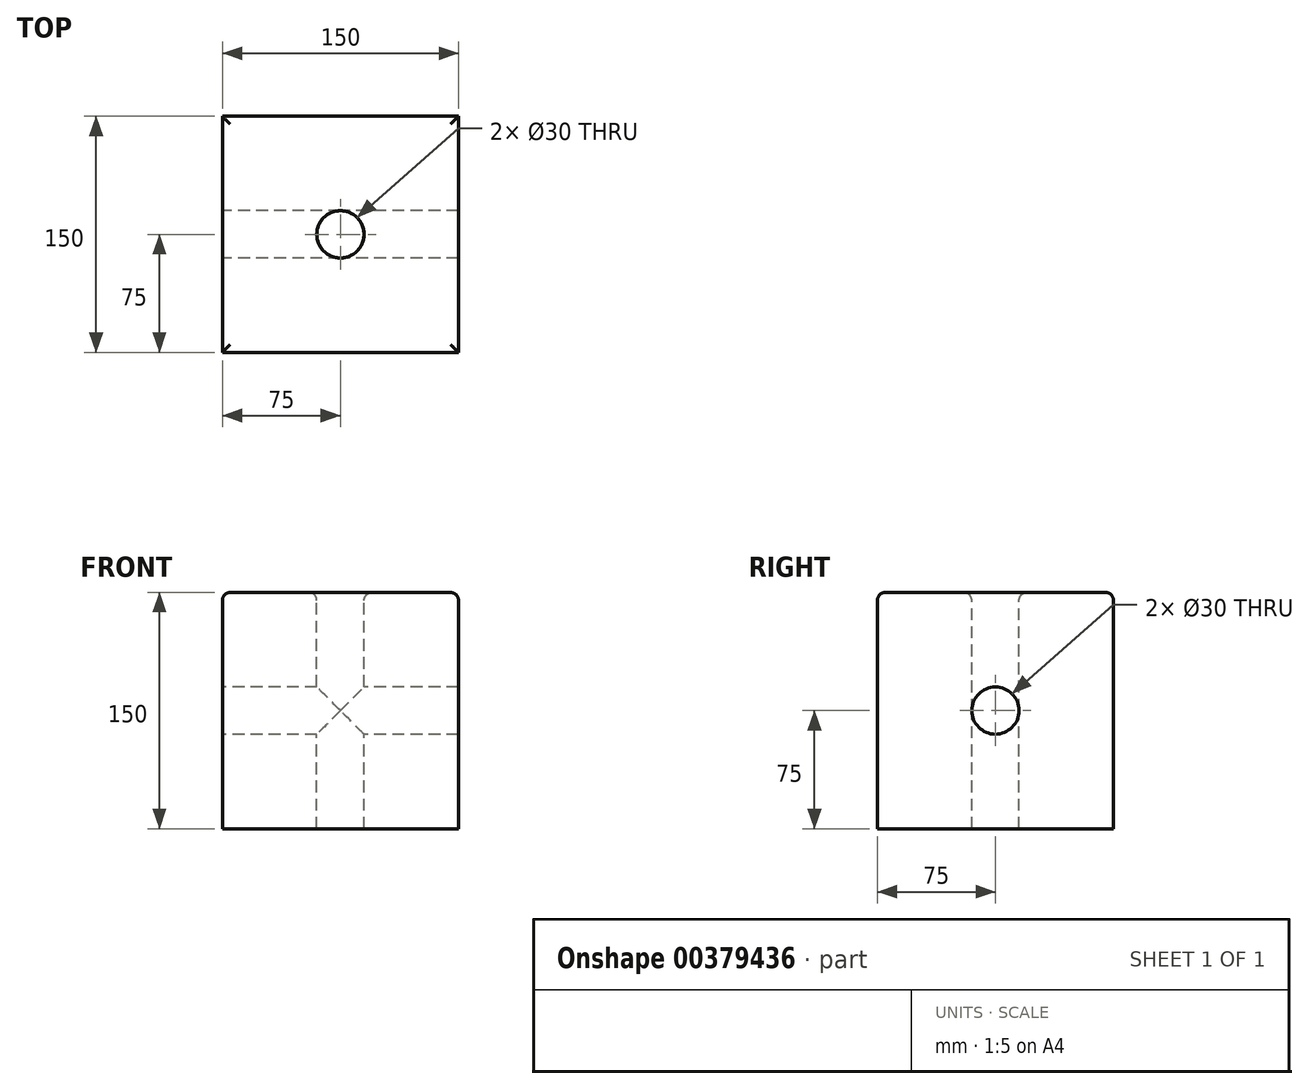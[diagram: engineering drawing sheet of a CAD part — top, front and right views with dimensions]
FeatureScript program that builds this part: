
annotation { "Feature Type Name" : "Feature", "Feature Type Description" : "" }
export const myFeature = defineFeature(function(context is Context, id is Id, definition is map)
    precondition{}
    {
        {
            var Q0;
            Q0=qCreatedBy(makeId("Front.planeOp"),FACE);
            var sketch = newSketch(context, id + "F0", { "sketchPlane" : qUnion([Q0])});
            skLineSegment(sketch, "E0.bottom", {"start": v(75, 75) * mm, "end": v(-75, 75) * mm});
            skLineSegment(sketch, "E0.top", {"start": v(75, -75) * mm, "end": v(-75, -75) * mm});
            skLineSegment(sketch, "E0.left", {"start": v(75, 75) * mm, "end": v(75, -75) * mm});
            skLineSegment(sketch, "E0.right", {"start": v(-75, 75) * mm, "end": v(-75, -75) * mm});
            skPoint(sketch, "E0.middle", {"position": v(0, 0) * mm});
            skSolve(sketch);
        }
        {
            var Q0;
            Q0 = qSketchRegion(id + "F0", true);
            extrude(context, id + "F1", {"entities" : qUnion([Q0]), "depth" : 150 * mm});
        }
        {
            var Q0;
            Q0=makeQuery(id+"F1.opExtrude","SWEPT_FACE",FACE,{"disambiguationData":[OSD([sQuery(id+"F0.wireOp",EDGE,"E0.bottom")])]});
            var sketch = newSketch(context, id + "F2", { "sketchPlane" : qUnion([Q0])});
            skCircle(sketch, "E1", {"center": v(0, -75) * mm, "radius": 15 * mm});
            skPoint(sketch, "E1.centerSnap0", {"position": v(-75, -75) * mm});
            skSolve(sketch);
        }
        {
            var Q0;
            Q0 = qSketchRegion(id + "F2", true);
            extrude(context, id + "F3", {"entities" : qUnion([Q0]), "operationType" : NewBodyOperationType.REMOVE, "oppositeDirection" : true, "depth" : 150 * mm});
        }
        {
            var Q0;
            Q0=makeQuery(id+"F1.opExtrude","SWEPT_FACE",FACE,{"disambiguationData":[OSD([sQuery(id+"F0.wireOp",EDGE,"E0.right")])]});
            var sketch = newSketch(context, id + "F4", { "sketchPlane" : qUnion([Q0])});
            skCircle(sketch, "E2", {"center": v(75, 0) * mm, "radius": 15 * mm});
            skPoint(sketch, "E2.centerSnap0", {"position": v(75, 75) * mm});
            skSolve(sketch);
        }
        {
            var Q0;
            Q0 = qSketchRegion(id + "F4", true);
            extrude(context, id + "F5", {"entities" : qUnion([Q0]), "operationType" : NewBodyOperationType.REMOVE, "oppositeDirection" : true, "depth" : 150 * mm});
        }
        {
            var Q0;
            Q0=makeQuery(id+"F1.opExtrude","SWEPT_FACE",FACE,{"disambiguationData":[OSD([sQuery(id+"F0.wireOp",EDGE,"E0.bottom")])]});
            fillet(context, id + "F6", {"entities" : qUnion([Q0]), "radius" : 5 * mm, "tangentPropagation" : true, "allowEdgeOverflow" : false});
        }
    });
